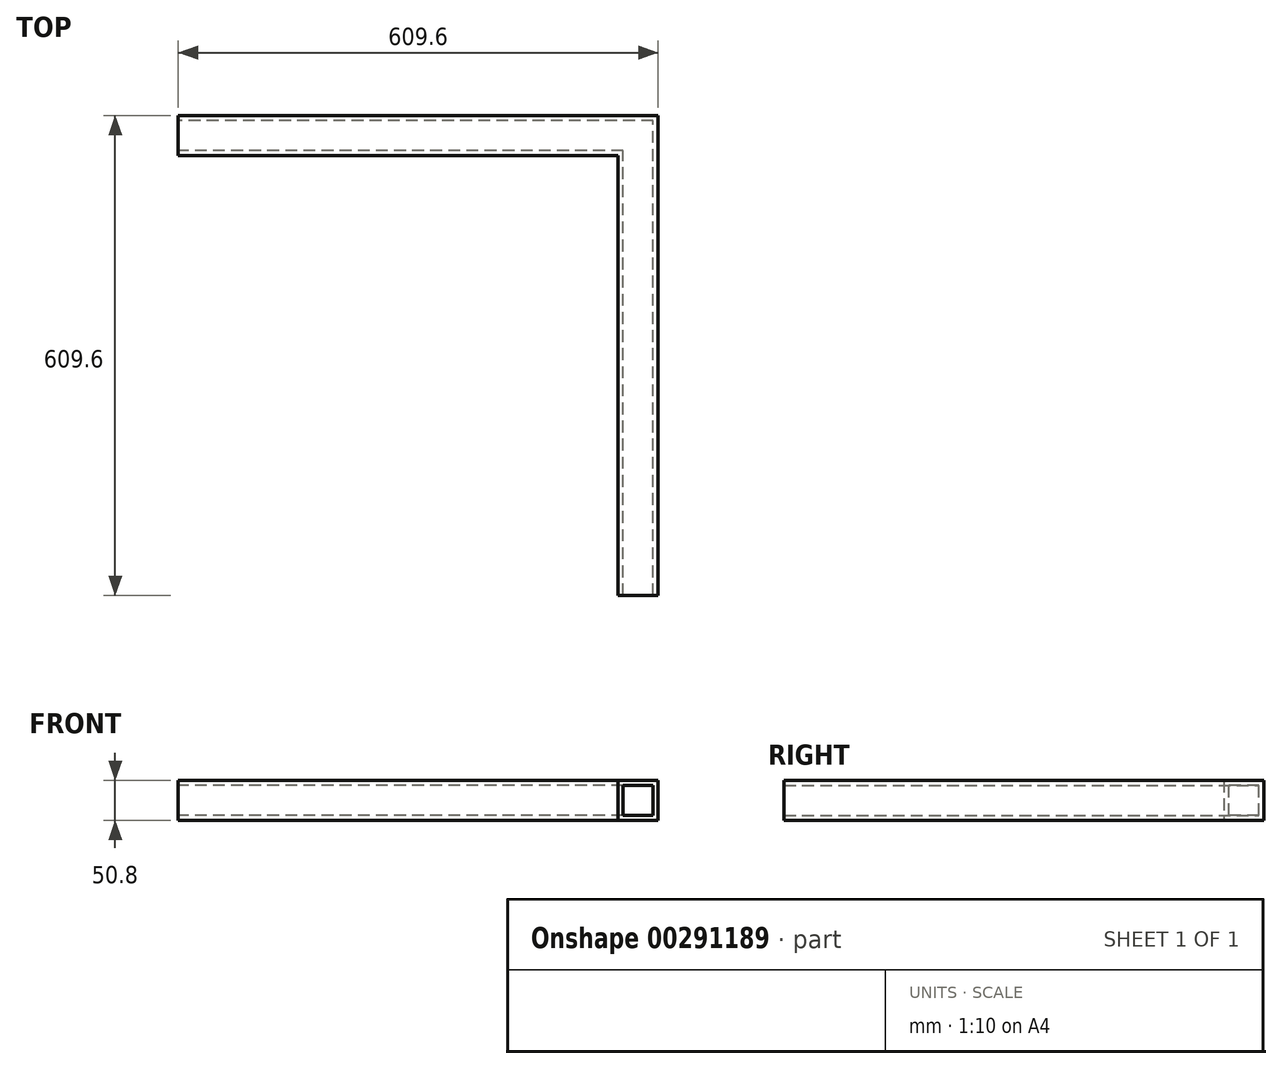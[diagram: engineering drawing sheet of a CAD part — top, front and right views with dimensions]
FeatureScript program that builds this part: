
annotation { "Feature Type Name" : "Feature", "Feature Type Description" : "" }
export const myFeature = defineFeature(function(context is Context, id is Id, definition is map)
    precondition{}
    {
        {
            var Q0;
            Q0=qCreatedBy(makeId("Top.planeOp"),FACE);
            var sketch = newSketch(context, id + "F0", { "sketchPlane" : qUnion([Q0])});
            skLineSegment(sketch, "E0", {"start": v(0, 0) * mm, "end": v(0, 584.2) * mm});
            skLineSegment(sketch, "E1", {"start": v(0, 584.2) * mm, "end": v(-584.2, 584.2) * mm});
            skSolve(sketch);
        }
        {
            var Q0;
            Q0=qCreatedBy(makeId("Front.planeOp"),FACE);
            var sketch = newSketch(context, id + "F1", { "sketchPlane" : qUnion([Q0])});
            skLineSegment(sketch, "E2.bottom", {"start": v(25.4, -25.4) * mm, "end": v(-25.4, -25.4) * mm});
            skLineSegment(sketch, "E2.top", {"start": v(25.4, 25.4) * mm, "end": v(-25.4, 25.4) * mm});
            skLineSegment(sketch, "E2.left", {"start": v(25.4, -25.4) * mm, "end": v(25.4, 25.4) * mm});
            skLineSegment(sketch, "E2.right", {"start": v(-25.4, -25.4) * mm, "end": v(-25.4, 25.4) * mm});
            skPoint(sketch, "E2.middle", {"position": v(0, 0) * mm});
            skLineSegment(sketch, "E3.0", {"start": v(19.05, 19.05) * mm, "end": v(-19.05, 19.05) * mm});
            skLineSegment(sketch, "E3.1", {"start": v(19.05, -19.05) * mm, "end": v(19.05, 19.05) * mm});
            skLineSegment(sketch, "E3.2", {"start": v(19.05, -19.05) * mm, "end": v(-19.05, -19.05) * mm});
            skLineSegment(sketch, "E3.3", {"start": v(-19.05, -19.05) * mm, "end": v(-19.05, 19.05) * mm});
            skSolve(sketch);
        }
        {
            var Q0;
            Q0=qSketchRegion(id+"F1",true);
            var Q1;
            Q1=qConstructionFilter(qBodyType(qCreatedBy(id+"F0",EDGE),BodyType.WIRE),ConstructionObject.NO);
            sweep(context, id + "F2", {"profiles" : qUnion([Q0]), "path" : qUnion([Q1])});
        }
    });
